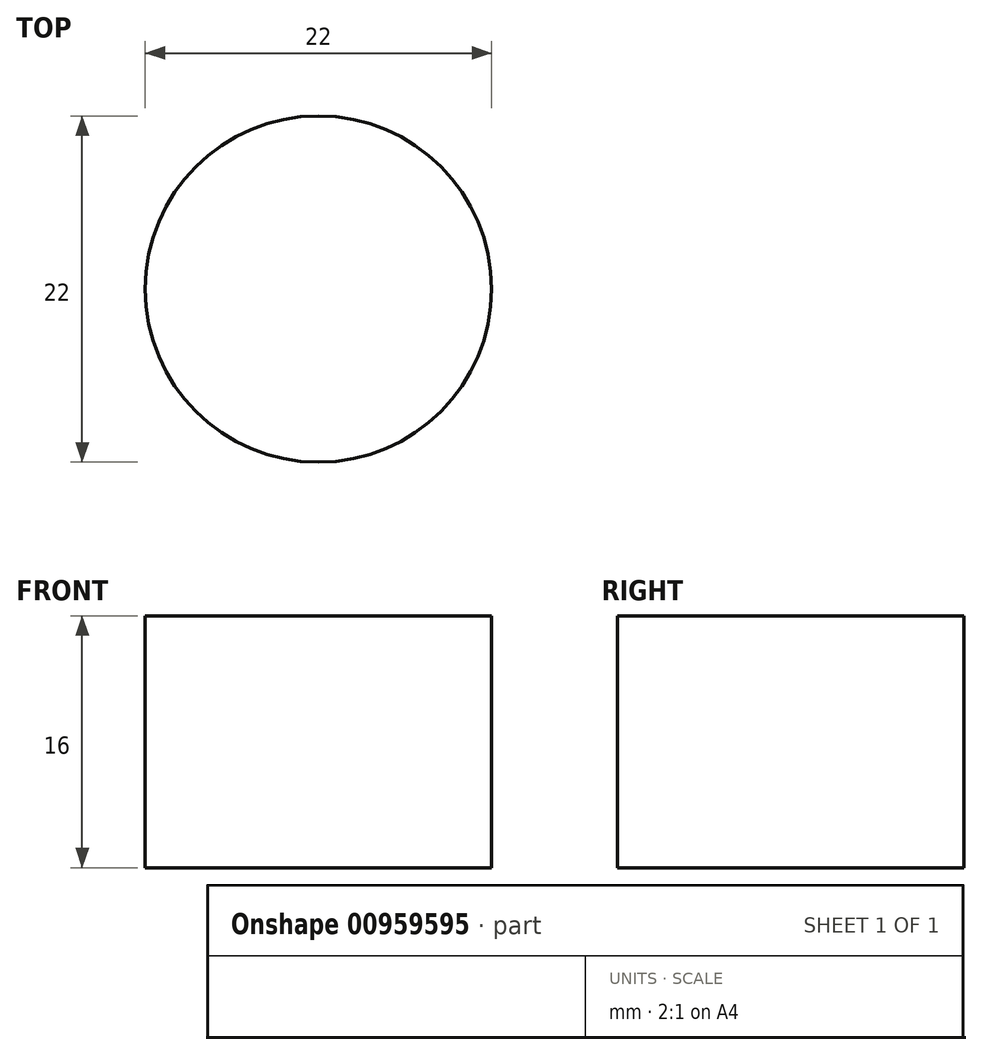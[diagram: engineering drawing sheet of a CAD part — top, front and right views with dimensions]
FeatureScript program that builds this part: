
annotation { "Feature Type Name" : "Feature", "Feature Type Description" : "" }
export const myFeature = defineFeature(function(context is Context, id is Id, definition is map)
    precondition{}
    {
        {
            var Q0;
            Q0=qCreatedBy(makeId("Top.planeOp"),FACE);
            var sketch = newSketch(context, id + "F0", { "sketchPlane" : qUnion([Q0])});
            skCircle(sketch, "E0", {"center": v(0, 0) * mm, "radius": 11 * mm});
            skSolve(sketch);
        }
        {
            var Q0;
            Q0 = qSketchRegion(id + "F0", true);
            extrude(context, id + "F1", {"entities" : qUnion([Q0]), "depth" : 16 * mm, "offsetDistance" : 25 * mm});
        }
    });
